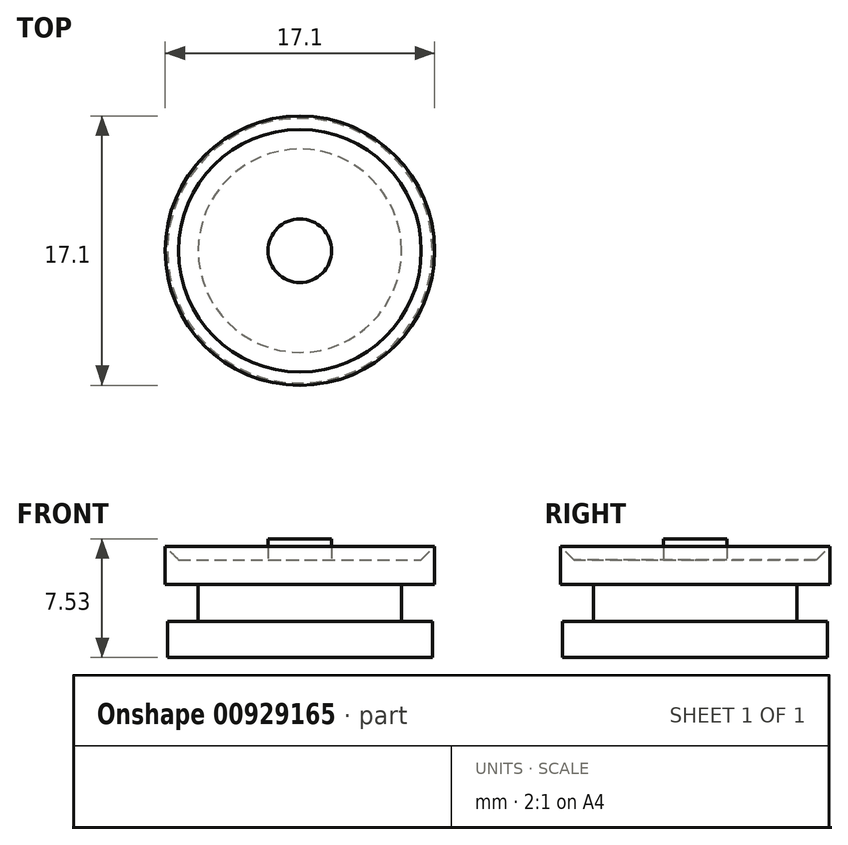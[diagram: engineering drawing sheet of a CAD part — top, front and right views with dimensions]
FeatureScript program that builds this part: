
annotation { "Feature Type Name" : "Feature", "Feature Type Description" : "" }
export const myFeature = defineFeature(function(context is Context, id is Id, definition is map)
    precondition{}
    {
        {
            var Q0;
            Q0=qCreatedBy(makeId("Front.planeOp"),FACE);
            var sketch = newSketch(context, id + "F0", { "sketchPlane" : qUnion([Q0])});
            skLineSegment(sketch, "E0", {"start": v(0, 2.77) * mm, "end": v(0, 9.97) * mm});
            skLineSegment(sketch, "E1", {"start": v(0, 9.97) * mm, "end": v(-2.02, 9.97) * mm});
            skLineSegment(sketch, "E2", {"start": v(-2.02, 9.97) * mm, "end": v(-2.02, 8.64) * mm});
            skLineSegment(sketch, "E3", {"start": v(-2.02, 8.64) * mm, "end": v(-6.45, 8.64) * mm});
            skLineSegment(sketch, "E4", {"start": v(-6.45, 8.64) * mm, "end": v(-6.45, 9.92) * mm});
            skLineSegment(sketch, "E5", {"start": v(-6.45, 9.92) * mm, "end": v(-8.55, 9.92) * mm});
            skLineSegment(sketch, "E6", {"start": v(-8.55, 9.92) * mm, "end": v(-8.55, 7.06) * mm});
            skLineSegment(sketch, "E7", {"start": v(-8.55, 7.06) * mm, "end": v(-6.45, 7.06) * mm});
            skLineSegment(sketch, "E8", {"start": v(-6.45, 7.06) * mm, "end": v(-6.45, 4.73) * mm});
            skLineSegment(sketch, "E9", {"start": v(-6.45, 4.73) * mm, "end": v(-8.4, 4.73) * mm});
            skLineSegment(sketch, "E10", {"start": v(-8.4, 4.73) * mm, "end": v(-8.4, 2.44) * mm});
            skLineSegment(sketch, "E11", {"start": v(-8.4, 2.44) * mm, "end": v(0, 2.44) * mm});
            skLineSegment(sketch, "E12", {"start": v(0, 2.44) * mm, "end": v(0, 2.77) * mm});
            skSolve(sketch);
        }
        {
            var Q0;
            Q0=makeQuery(id+"F0.imprint","IMPRINT",FACE,{"disambiguationData":[TD([[makeQuery(id+"F0.imprint","IMPRINT",EDGE,{"derivedFrom":sQuery(id+"F0.wireOp",EDGE,"E0")}),1.0]])]});
            var Q1;
            Q1=sQuery(id+"F0.wireOp",EDGE,"E0");
            revolve(context, id + "F1", {"surfaceOperationType" : NewSurfaceOperationType.NEW, "entities" : qUnion([Q0]), "axis" : qUnion([Q1]), "revolveType" : RevolveType.FULL});
        }
        {
            var Q0;
            Q0=makeQuery(id+"F1.opRevolve","SWEPT_EDGE",EDGE,{"disambiguationData":[OSD([sQuery(id+"F0.wireOp",EDGE,"E4"),sQuery(id+"F0.wireOp",EDGE,"E5")])]});
            chamfer(context, id + "F2", {"entities" : qUnion([Q0]), "width" : 2.54 * mm, "tangentPropagation" : true});
        }
    });
